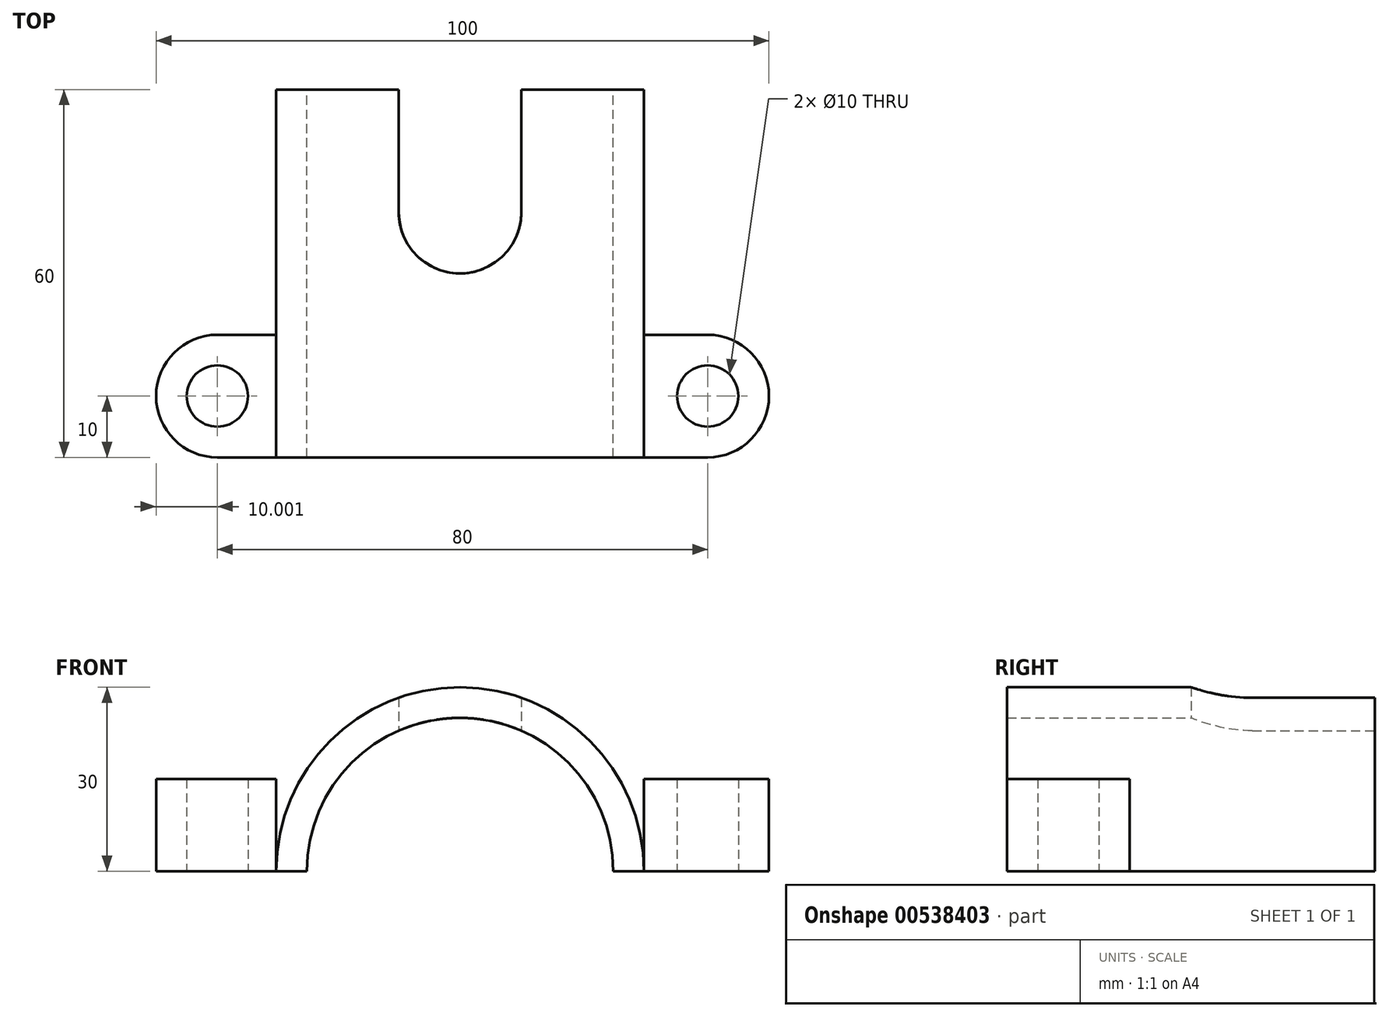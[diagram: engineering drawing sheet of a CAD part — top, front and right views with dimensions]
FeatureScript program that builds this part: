
annotation { "Feature Type Name" : "Feature", "Feature Type Description" : "" }
export const myFeature = defineFeature(function(context is Context, id is Id, definition is map)
    precondition{}
    {
        {
            var Q0;
            Q0=qCreatedBy(makeId("Front.planeOp"),FACE);
            var sketch = newSketch(context, id + "F0", { "sketchPlane" : qUnion([Q0])});
            skArc(sketch, "E0", {"start": v(30, 0) * mm, "mid": v(0, 30) * mm, "end": v(-30, 0) * mm});
            skLineSegment(sketch, "E1", {"start": v(30, 0) * mm, "end": v(25, 0) * mm});
            skArc(sketch, "E2", {"start": v(25, 0) * mm, "mid": v(0, 25) * mm, "end": v(-25, 0) * mm});
            skLineSegment(sketch, "E3", {"start": v(-30, 0) * mm, "end": v(-25, 0) * mm});
            skSolve(sketch);
        }
        {
            var Q0;
            Q0=makeQuery(id+"F0.imprint","IMPRINT",FACE,{"disambiguationData":[TD([[makeQuery(id+"F0.imprint","IMPRINT",EDGE,{"derivedFrom":sQuery(id+"F0.wireOp",EDGE,"E0")}),1.0]])]});
            extrude(context, id + "F1", {"entities" : qUnion([Q0]), "depth" : 60 * mm, "offsetDistance" : 25 * mm});
        }
        {
            var Q0;
            Q0=qCreatedBy(makeId("Top.planeOp"),FACE);
            var sketch = newSketch(context, id + "F2", { "sketchPlane" : qUnion([Q0])});
            skLineSegment(sketch, "E4.bottom", {"start": v(-10, -20) * mm, "end": v(10, -20) * mm});
            skLineSegment(sketch, "E4.top", {"start": v(-10, 20) * mm, "end": v(10, 20) * mm});
            skLineSegment(sketch, "E4.left", {"start": v(-10, -20) * mm, "end": v(-10, 20) * mm});
            skLineSegment(sketch, "E4.right", {"start": v(10, -20) * mm, "end": v(10, 20) * mm});
            skPoint(sketch, "E4.middle", {"position": v(0, 0) * mm});
            skArc(sketch, "E5", {"start": v(-10, -20) * mm, "mid": v(0, -30) * mm, "end": v(10, -20) * mm});
            skSolve(sketch);
        }
        {
            var Q0;
            Q0=qSketchRegion(id+"F2",true);
            extrude(context, id + "F3", {"entities" : qUnion([Q0]), "operationType" : NewBodyOperationType.REMOVE, "endBound" : BoundingType.THROUGH_ALL, "depth" : 25 * mm, "offsetDistance" : 25 * mm});
        }
        {
            var Q0;
            Q0=qCreatedBy(makeId("Top.planeOp"),FACE);
            var sketch = newSketch(context, id + "F4", { "sketchPlane" : qUnion([Q0])});
            skLineSegment(sketch, "E6.bottom", {"start": v(-39.59, -40) * mm, "end": v(-30, -40) * mm});
            skLineSegment(sketch, "E6.top", {"start": v(-39.59, -60) * mm, "end": v(-30, -60) * mm});
            skLineSegment(sketch, "E6.left", {"start": v(-39.59, -40) * mm, "end": v(-39.59, -60) * mm});
            skLineSegment(sketch, "E6.right", {"start": v(-30, -40) * mm, "end": v(-30, -60) * mm});
            skPoint(sketch, "E6.middle", {"position": v(-34.8, -50) * mm});
            skLineSegment(sketch, "E7.bottom", {"start": v(40.41, -40) * mm, "end": v(30, -40) * mm});
            skLineSegment(sketch, "E7.top", {"start": v(40.41, -60) * mm, "end": v(30, -60) * mm});
            skLineSegment(sketch, "E7.left", {"start": v(40.41, -40) * mm, "end": v(40.41, -60) * mm});
            skLineSegment(sketch, "E7.right", {"start": v(30, -40) * mm, "end": v(30, -60) * mm});
            skPoint(sketch, "E7.middle", {"position": v(35.2, -50) * mm});
            skArc(sketch, "E8", {"start": v(40.41, -60) * mm, "mid": v(50.41, -50) * mm, "end": v(40.41, -40) * mm});
            skArc(sketch, "E9", {"start": v(-39.59, -40) * mm, "mid": v(-49.59, -50) * mm, "end": v(-39.59, -60) * mm});
            skCircle(sketch, "E10", {"center": v(40.41, -50) * mm, "radius": 5 * mm});
            skCircle(sketch, "E11", {"center": v(-39.59, -50) * mm, "radius": 5 * mm});
            skSolve(sketch);
        }
        {
            var Q0;
            Q0=qSketchRegion(id+"F4",true);
            extrude(context, id + "F5", {"entities" : qUnion([Q0]), "depth" : 15 * mm, "offsetDistance" : 25 * mm});
        }
    });
